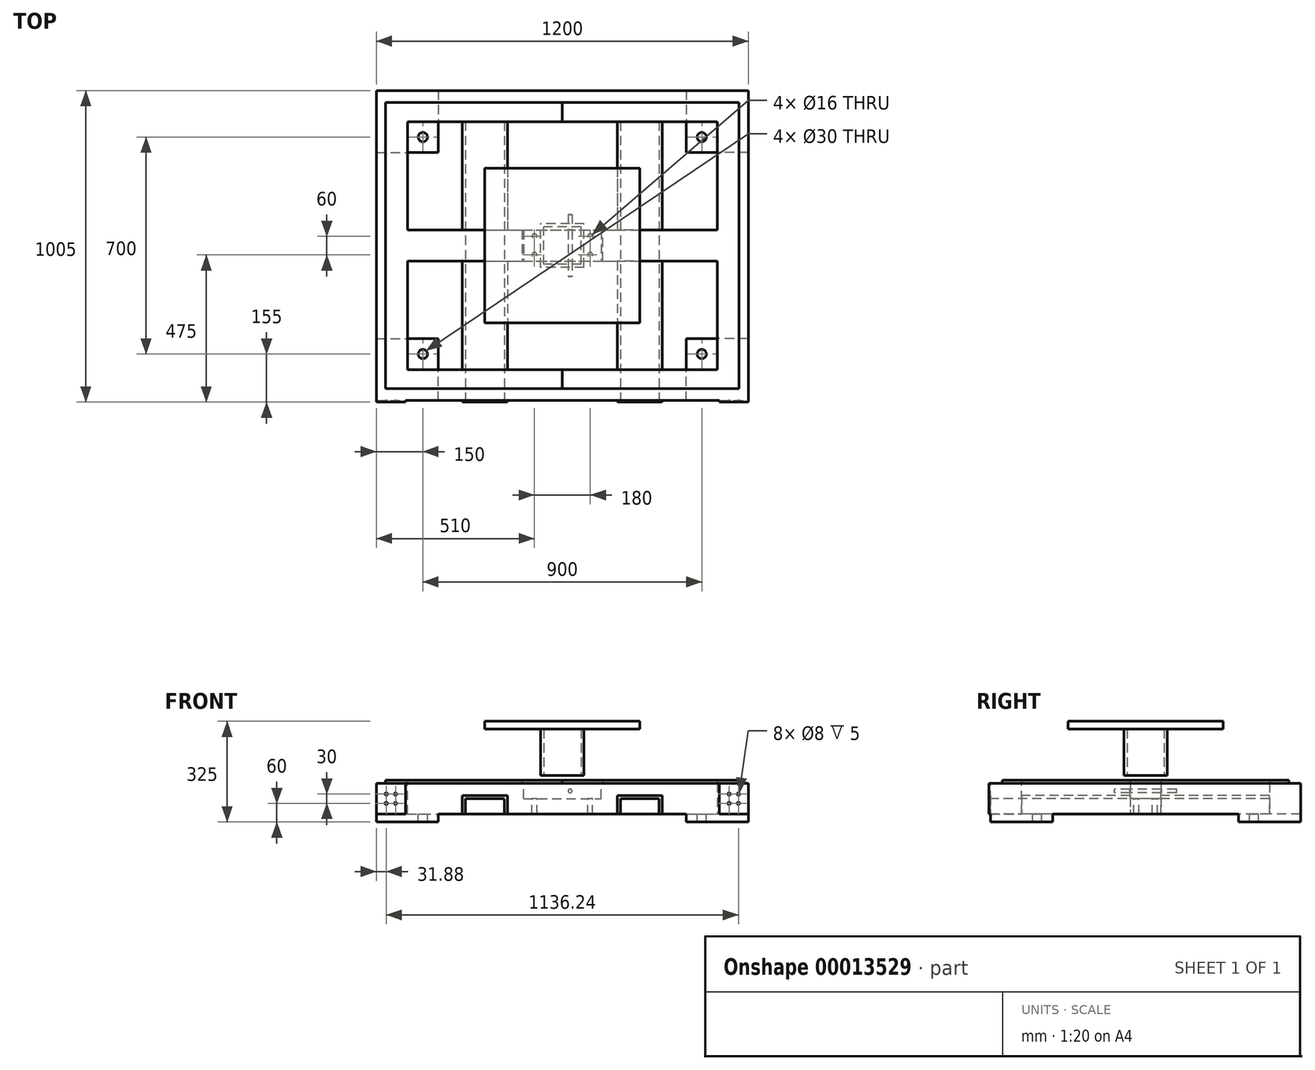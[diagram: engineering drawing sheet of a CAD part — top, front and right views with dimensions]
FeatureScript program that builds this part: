
annotation { "Feature Type Name" : "Feature", "Feature Type Description" : "" }
export const myFeature = defineFeature(function(context is Context, id is Id, definition is map)
    precondition{}
    {
        {
            var Q0;
            Q0=qCreatedBy(makeId("Top.planeOp"),FACE);
            var sketch = newSketch(context, id + "F0", { "sketchPlane" : qUnion([Q0])});
            skLineSegment(sketch, "E0.rect.bottom", {"start": v(-500, 50) * mm, "end": v(500, 50) * mm});
            skLineSegment(sketch, "E0.rect.top", {"start": v(-500, -50) * mm, "end": v(500, -50) * mm});
            skLineSegment(sketch, "E0.rect.left", {"start": v(-500, 50) * mm, "end": v(-500, -50) * mm});
            skLineSegment(sketch, "E0.rect.right", {"start": v(500, 50) * mm, "end": v(500, -50) * mm});
            skPoint(sketch, "E0.rect.middle", {"position": v(0, 0) * mm});
            skLineSegment(sketch, "E1", {"start": v(0, 0) * mm, "end": v(0, 499.4) * mm, "construction": true});
            skLineSegment(sketch, "E2", {"start": v(0, 0) * mm, "end": v(0, -436.12) * mm, "construction": true});
            skLineSegment(sketch, "E3", {"start": v(0, 450) * mm, "end": v(-502.35, 450) * mm, "construction": true});
            skLineSegment(sketch, "E4", {"start": v(0, 0) * mm, "end": v(-500, 0) * mm, "construction": true});
            skLineSegment(sketch, "E5", {"start": v(0, 0) * mm, "end": v(500, 0) * mm, "construction": true});
            skLineSegment(sketch, "E6.0.MirrorCS", {"start": v(0, -450) * mm, "end": v(-502.35, -450) * mm, "construction": true});
            skLineSegment(sketch, "E7.rect.bottom", {"start": v(-500, 400) * mm, "end": v(500, 400) * mm});
            skLineSegment(sketch, "E7.rect.top", {"start": v(-500, 500) * mm, "end": v(500, 500) * mm});
            skLineSegment(sketch, "E7.rect.left", {"start": v(-500, 400) * mm, "end": v(-500, 500) * mm});
            skLineSegment(sketch, "E7.rect.right", {"start": v(500, 400) * mm, "end": v(500, 500) * mm});
            skPoint(sketch, "E7.rect.middle", {"position": v(0, 450) * mm});
            skLineSegment(sketch, "E8.rect.bottom", {"start": v(-500, -400) * mm, "end": v(500, -400) * mm});
            skLineSegment(sketch, "E8.rect.top", {"start": v(-500, -500) * mm, "end": v(500, -500) * mm});
            skLineSegment(sketch, "E8.rect.left", {"start": v(-500, -400) * mm, "end": v(-500, -500) * mm});
            skLineSegment(sketch, "E8.rect.right", {"start": v(500, -400) * mm, "end": v(500, -500) * mm});
            skPoint(sketch, "E8.rect.middle", {"position": v(0, -450) * mm});
            skLineSegment(sketch, "E9", {"start": v(-500, 500) * mm, "end": v(-500, -512.7) * mm, "construction": true});
            skLineSegment(sketch, "E10", {"start": v(500, 500) * mm, "end": v(500, -500) * mm, "construction": true});
            skLineSegment(sketch, "E11", {"start": v(-500, 400) * mm, "end": v(-600, 500) * mm});
            skLineSegment(sketch, "E12", {"start": v(-600, 500) * mm, "end": v(-500, 500) * mm});
            skLineSegment(sketch, "E13.1.MirrorCS", {"start": v(500, 400) * mm, "end": v(600, 500) * mm});
            skLineSegment(sketch, "E13.2.MirrorCS", {"start": v(600, 500) * mm, "end": v(500, 500) * mm});
            skLineSegment(sketch, "E14.1.MirrorCS", {"start": v(-500, -400) * mm, "end": v(-600, -500) * mm});
            skLineSegment(sketch, "E14.2.MirrorCS", {"start": v(-600, -500) * mm, "end": v(-500, -500) * mm});
            skLineSegment(sketch, "E15.1.MirrorCS", {"start": v(500, -400) * mm, "end": v(600, -500) * mm});
            skLineSegment(sketch, "E15.3.MirrorCS", {"start": v(600, -500) * mm, "end": v(500, -500) * mm});
            skLineSegment(sketch, "E16", {"start": v(-600, 500) * mm, "end": v(-600, -500) * mm});
            skLineSegment(sketch, "E17", {"start": v(-500, -400) * mm, "end": v(-500, 400) * mm});
            skLineSegment(sketch, "E18", {"start": v(500, 400) * mm, "end": v(500, -400) * mm});
            skLineSegment(sketch, "E19", {"start": v(600, -500) * mm, "end": v(600, 500) * mm});
            skLineSegment(sketch, "E20", {"start": v(-500, 400) * mm, "end": v(-250, 400) * mm});
            skLineSegment(sketch, "E21", {"start": v(-250, 400) * mm, "end": v(-250, 352.87) * mm});
            skSolve(sketch);
        }
        {
            var Q0;
            {var subQ1=sQuery(id+"F0.wireOp",EDGE,"E11");Q0=makeQuery(id+"F0.imprint","IMPRINT",FACE,{"disambiguationData":[TD([[makeQuery(id+"F0.imprint","IMPRINT",EDGE,{"derivedFrom":subQ1}),1.0]])]});}
            extrude(context, id + "F1", {"entities" : qUnion([Q0]), "endBound" : BoundingType.SYMMETRIC, "oppositeDirection" : true, "depth" : 100 * mm});
        }
        {
            var Q0;
            {var subQ4=sQuery(id+"F0.wireOp",EDGE,"E13.1.MirrorCS");Q0=makeQuery(id+"F0.imprint","IMPRINT",FACE,{"disambiguationData":[TD([[makeQuery(id+"F0.imprint","IMPRINT",EDGE,{"derivedFrom":subQ4}),-1.0]])]});}
            extrude(context, id + "F2", {"entities" : qUnion([Q0]), "endBound" : BoundingType.SYMMETRIC, "depth" : 100 * mm});
        }
        {
            var Q0;
            Q0=makeQuery(id+"F0.imprint","IMPRINT",FACE,{"disambiguationData":[TD([[makeQuery(id+"F0.imprint","IMPRINT",EDGE,{"derivedFrom":sQuery(id+"F0.wireOp",EDGE,"E8.rect.bottom")}),-1.0]])]});
            var Q1;
            Q1=makeQuery(id+"F0.imprint","IMPRINT",FACE,{"disambiguationData":[TD([[makeQuery(id+"F0.imprint","IMPRINT",EDGE,{"derivedFrom":sQuery(id+"F0.wireOp",EDGE,"E8.rect.left")}),-1.0]])]});
            var Q2;
            Q2=makeQuery(id+"F0.imprint","IMPRINT",FACE,{"disambiguationData":[TD([[makeQuery(id+"F0.imprint","IMPRINT",EDGE,{"derivedFrom":sQuery(id+"F0.wireOp",EDGE,"E15.1.MirrorCS")}),-1.0]])]});
            extrude(context, id + "F3", {"entities" : qUnion([Q0, Q1, Q2]), "endBound" : BoundingType.SYMMETRIC, "depth" : 100 * mm});
        }
        {
            var Q0;
            Q0=makeQuery(id+"F0.imprint","IMPRINT",FACE,{"disambiguationData":[TD([[makeQuery(id+"F0.imprint","IMPRINT",EDGE,{"derivedFrom":sQuery(id+"F0.wireOp",EDGE,"E7.rect.bottom")}),1.0]])]});
            var Q1;
            Q1=makeQuery(id+"F0.imprint","IMPRINT",FACE,{"disambiguationData":[TD([[makeQuery(id+"F0.imprint","IMPRINT",EDGE,{"derivedFrom":sQuery(id+"F0.wireOp",EDGE,"E7.rect.left")}),1.0]])]});
            var Q2;
            Q2=makeQuery(id+"F0.imprint","IMPRINT",FACE,{"disambiguationData":[TD([[makeQuery(id+"F0.imprint","IMPRINT",EDGE,{"derivedFrom":sQuery(id+"F0.wireOp",EDGE,"E7.rect.right")}),-1.0]])]});
            extrude(context, id + "F4", {"entities" : qUnion([Q0, Q1, Q2]), "endBound" : BoundingType.SYMMETRIC, "depth" : 100 * mm});
        }
        {
            var Q0;
            {var subQ2=sQuery(id+"F0.wireOp",EDGE,"E0.rect.bottom");Q0=makeQuery(id+"F0.imprint","IMPRINT",FACE,{"disambiguationData":[TD([[makeQuery(id+"F0.imprint","IMPRINT",EDGE,{"derivedFrom":subQ2}),-1.0]])]});}
            extrude(context, id + "F5", {"entities" : qUnion([Q0]), "endBound" : BoundingType.SYMMETRIC, "depth" : 100 * mm});
        }
        {
            var Q0;
            Q0=makeQuery(id+"F3.opExtrude","SWEPT_FACE",FACE,{"disambiguationData":[OSD([sQuery(id+"F0.wireOp",EDGE,"E8.rect.top"),sQuery(id+"F0.wireOp",EDGE,"E14.2.MirrorCS"),sQuery(id+"F0.wireOp",EDGE,"E15.3.MirrorCS")])]});
            var sketch = newSketch(context, id + "F6", { "sketchPlane" : qUnion([Q0])});
            skLineSegment(sketch, "E22", {"start": v(-187.5, -50) * mm, "end": v(-187.5, 0) * mm});
            skLineSegment(sketch, "E23", {"start": v(-187.5, 0) * mm, "end": v(-312.5, 0) * mm});
            skLineSegment(sketch, "E24", {"start": v(-312.5, 0) * mm, "end": v(-312.5, -50) * mm});
            skLineSegment(sketch, "E25.0", {"start": v(-322.5, 0) * mm, "end": v(-322.5, -50) * mm});
            skLineSegment(sketch, "E26.0", {"start": v(-177.5, -50) * mm, "end": v(-177.5, 0) * mm});
            skLineSegment(sketch, "E27", {"start": v(-322.5, 0) * mm, "end": v(-322.5, 10) * mm});
            skLineSegment(sketch, "E28", {"start": v(-177.5, 0) * mm, "end": v(-177.5, 10) * mm});
            skLineSegment(sketch, "E29", {"start": v(-322.5, -50) * mm, "end": v(-312.5, -50) * mm});
            skLineSegment(sketch, "E30", {"start": v(-187.5, -50) * mm, "end": v(-177.5, -50) * mm});
            skLineSegment(sketch, "E31", {"start": v(-177.5, 10) * mm, "end": v(-322.5, 10) * mm});
            skLineSegment(sketch, "E32", {"start": v(0, -50) * mm, "end": v(0, 50) * mm, "construction": true});
            skLineSegment(sketch, "E33.0.MirrorCS", {"start": v(177.5, 0) * mm, "end": v(177.5, 10) * mm});
            skLineSegment(sketch, "E33.1.MirrorCS", {"start": v(322.5, 0) * mm, "end": v(322.5, 10) * mm});
            skLineSegment(sketch, "E33.2.MirrorCS", {"start": v(322.5, -50) * mm, "end": v(312.5, -50) * mm});
            skLineSegment(sketch, "E33.3.MirrorCS", {"start": v(187.5, -50) * mm, "end": v(177.5, -50) * mm});
            skLineSegment(sketch, "E33.4.MirrorCS", {"start": v(322.5, 0) * mm, "end": v(322.5, -50) * mm});
            skLineSegment(sketch, "E33.5.MirrorCS", {"start": v(312.5, 0) * mm, "end": v(312.5, -50) * mm});
            skLineSegment(sketch, "E33.6.MirrorCS", {"start": v(177.5, 10) * mm, "end": v(322.5, 10) * mm});
            skLineSegment(sketch, "E33.7.MirrorCS", {"start": v(187.5, 0) * mm, "end": v(312.5, 0) * mm});
            skLineSegment(sketch, "E33.8.MirrorCS", {"start": v(187.5, -50) * mm, "end": v(187.5, 0) * mm});
            skLineSegment(sketch, "E33.9.MirrorCS", {"start": v(177.5, -50) * mm, "end": v(177.5, 0) * mm});
            skSolve(sketch);
        }
        {
            var Q0;
            {var subQ2=sQuery(id+"F6.wireOp",EDGE,"E22");Q0=makeQuery(id+"F6.imprint","IMPRINT",FACE,{"disambiguationData":[TD([[makeQuery(id+"F6.imprint","IMPRINT",EDGE,{"derivedFrom":subQ2}),1.0]])]});}
            var Q1;
            {var subQ2=sQuery(id+"F6.wireOp",EDGE,"E33.5.MirrorCS");Q1=makeQuery(id+"F6.imprint","IMPRINT",FACE,{"disambiguationData":[TD([[makeQuery(id+"F6.imprint","IMPRINT",EDGE,{"derivedFrom":subQ2}),-1.0]])]});}
            var Q2;
            Q2=makeQuery(id+"F4.opExtrude","SWEPT_FACE",FACE,{"disambiguationData":[OSD([sQuery(id+"F0.wireOp",EDGE,"E7.rect.bottom"),sQuery(id+"F0.wireOp",EDGE,"E20")])]});
            extrude(context, id + "F7", {"entities" : qUnion([Q0, Q1]), "operationType" : NewBodyOperationType.REMOVE, "endBound" : BoundingType.UP_TO_SURFACE, "oppositeDirection" : true, "endBoundEntityFace" : qUnion([Q2]), "depth" : mm});
        }
        {
            var Q0;
            Q0=makeQuery(id+"F6.imprint","IMPRINT",FACE,{"disambiguationData":[TD([[makeQuery(id+"F6.imprint","IMPRINT",EDGE,{"derivedFrom":sQuery(id+"F6.wireOp",EDGE,"E33.0.MirrorCS")}),-1.0]])]});
            var Q1;
            Q1=makeQuery(id+"F6.imprint","IMPRINT",FACE,{"disambiguationData":[TD([[makeQuery(id+"F6.imprint","IMPRINT",EDGE,{"derivedFrom":sQuery(id+"F6.wireOp",EDGE,"E22")}),-1.0]])]});
            var Q2;
            Q2=makeQuery(id+"F4.opExtrude","SWEPT_FACE",FACE,{"disambiguationData":[OSD([sQuery(id+"F0.wireOp",EDGE,"E7.rect.bottom"),sQuery(id+"F0.wireOp",EDGE,"E20")])]});
            extrude(context, id + "F8", {"entities" : qUnion([Q0, Q1]), "endBound" : BoundingType.UP_TO_SURFACE, "oppositeDirection" : true, "endBoundEntityFace" : qUnion([Q2]), "depth" : 25 * mm, "hasSecondDirection" : true, "secondDirectionOppositeDirection" : false, "secondDirectionDepth" : 5 * mm});
        }
        {
            var Q0;
            Q0=makeQuery(id+"F8.opExtrude","SWEPT_BODY",BODY,{"disambiguationData":[OSD([sQuery(id+"F6.wireOp",EDGE,"E22"),sQuery(id+"F6.wireOp",EDGE,"E23"),sQuery(id+"F6.wireOp",EDGE,"E24"),sQuery(id+"F6.wireOp",EDGE,"E25.0"),sQuery(id+"F6.wireOp",EDGE,"E26.0"),sQuery(id+"F6.wireOp",EDGE,"E27"),sQuery(id+"F6.wireOp",EDGE,"E28"),sQuery(id+"F6.wireOp",EDGE,"E29"),sQuery(id+"F6.wireOp",EDGE,"E30"),sQuery(id+"F6.wireOp",EDGE,"E31")])]});
            var Q1;
            Q1=qCreatedBy(makeId("Right.planeOp"),FACE);
            mirror(context, id + "F9", {"operationType" : NewBodyOperationType.ADD, "entities" : qUnion([Q0]), "mirrorPlane" : qUnion([Q1])});
        }
        {
            var Q0;
            {var subQ0=sQuery(id+"F6.wireOp",EDGE,"E23");var subQ1=sQuery(id+"F6.wireOp",EDGE,"E24");var subQ2=makeQuery(id+"F7.opExtrude","SWEPT_EDGE",EDGE,{"disambiguationData":[OSD([subQ0,subQ1])]});Q0=makeQuery(id+"F9.boolean.opBoolean","MERGE",EDGE,{"derivedFrom":[makeQuery(id+"F7.boolean.opBoolean","COPY",EDGE,{"disambiguationData":[OD(0.0)],"derivedFrom":subQ2}),makeQuery(id+"F7.boolean.opBoolean","COPY",EDGE,{"disambiguationData":[OD(1.0)],"derivedFrom":subQ2}),makeQuery(id+"F8.opExtrude","SWEPT_EDGE",EDGE,{"disambiguationData":[OSD([subQ0,subQ1])]})]});}
            var Q1;
            {var subQ0=sQuery(id+"F6.wireOp",EDGE,"E22");var subQ1=sQuery(id+"F6.wireOp",EDGE,"E23");var subQ2=makeQuery(id+"F7.opExtrude","SWEPT_EDGE",EDGE,{"disambiguationData":[OSD([subQ0,subQ1])]});Q1=makeQuery(id+"F9.boolean.opBoolean","MERGE",EDGE,{"derivedFrom":[makeQuery(id+"F7.boolean.opBoolean","COPY",EDGE,{"disambiguationData":[OD(0.0)],"derivedFrom":subQ2}),makeQuery(id+"F7.boolean.opBoolean","COPY",EDGE,{"disambiguationData":[OD(1.0)],"derivedFrom":subQ2}),makeQuery(id+"F8.opExtrude","SWEPT_EDGE",EDGE,{"disambiguationData":[OSD([subQ0,subQ1])]})]});}
            var Q2;
            {var subQ0=makeQuery(id+"F7.opExtrude","SWEPT_EDGE",EDGE,{"disambiguationData":[OSD([sQuery(id+"F6.wireOp",EDGE,"E33.7.MirrorCS"),sQuery(id+"F6.wireOp",EDGE,"E33.8.MirrorCS")])]});Q2=makeQuery(id+"F9.boolean.opBoolean","MERGE",EDGE,{"derivedFrom":[makeQuery(id+"F7.boolean.opBoolean","COPY",EDGE,{"disambiguationData":[OD(0.0)],"derivedFrom":subQ0}),makeQuery(id+"F7.boolean.opBoolean","COPY",EDGE,{"disambiguationData":[OD(1.0)],"derivedFrom":subQ0}),makeQuery(id+"F9.opPattern","COPY",EDGE,{"derivedFrom":makeQuery(id+"F8.opExtrude","SWEPT_EDGE",EDGE,{"disambiguationData":[OSD([sQuery(id+"F6.wireOp",EDGE,"E22"),sQuery(id+"F6.wireOp",EDGE,"E23")])]}),"instanceName":"1"})]});}
            var Q3;
            {var subQ0=makeQuery(id+"F7.opExtrude","SWEPT_EDGE",EDGE,{"disambiguationData":[OSD([sQuery(id+"F6.wireOp",EDGE,"E33.5.MirrorCS"),sQuery(id+"F6.wireOp",EDGE,"E33.7.MirrorCS")])]});Q3=makeQuery(id+"F9.boolean.opBoolean","MERGE",EDGE,{"derivedFrom":[makeQuery(id+"F7.boolean.opBoolean","COPY",EDGE,{"disambiguationData":[OD(0.0)],"derivedFrom":subQ0}),makeQuery(id+"F7.boolean.opBoolean","COPY",EDGE,{"disambiguationData":[OD(1.0)],"derivedFrom":subQ0}),makeQuery(id+"F9.opPattern","COPY",EDGE,{"derivedFrom":makeQuery(id+"F8.opExtrude","SWEPT_EDGE",EDGE,{"disambiguationData":[OSD([sQuery(id+"F6.wireOp",EDGE,"E23"),sQuery(id+"F6.wireOp",EDGE,"E24")])]}),"instanceName":"1"})]});}
            fillet(context, id + "F10", {"entities" : qUnion([Q0, Q1, Q2, Q3]), "radius" : 3 * mm, "allowEdgeOverflow" : false});
        }
        {
            var Q0;
            {var subQ0=sQuery(id+"F0.wireOp",EDGE,"E8.rect.bottom");var subQ1=sQuery(id+"F0.wireOp",EDGE,"E8.rect.top");var subQ2=sQuery(id+"F0.wireOp",EDGE,"E14.1.MirrorCS");var subQ3=sQuery(id+"F0.wireOp",EDGE,"E14.2.MirrorCS");var subQ4=sQuery(id+"F0.wireOp",EDGE,"E15.3.MirrorCS");Q0=makeQuery(id+"F7.boolean.opBoolean","SPLIT",FACE,{"disambiguationData":[TD([makeQuery(id+"F3.opExtrude","SWEPT_FACE",FACE,{"disambiguationData":[OSD([subQ2])]})])],"derivedFrom":makeQuery(id+"F3.opExtrude","CAP_FACE",FACE,{"disambiguationData":[OSD([subQ0,subQ1,subQ2,subQ3,sQuery(id+"F0.wireOp",EDGE,"E15.1.MirrorCS"),subQ4])],"isStart":true})});}
            var sketch = newSketch(context, id + "F11", { "sketchPlane" : qUnion([Q0])});
            skLineSegment(sketch, "E34", {"start": v(0, 0) * mm, "end": v(0, 500) * mm, "construction": true});
            skLineSegment(sketch, "E35", {"start": v(0, 0) * mm, "end": v(-600, 0) * mm, "construction": true});
            skLineSegment(sketch, "E36.bottom", {"start": v(-600, 500) * mm, "end": v(-400, 500) * mm});
            skLineSegment(sketch, "E36.top", {"start": v(-600, 300) * mm, "end": v(-400, 300) * mm});
            skLineSegment(sketch, "E36.left", {"start": v(-600, 500) * mm, "end": v(-600, 300) * mm});
            skLineSegment(sketch, "E36.right", {"start": v(-400, 500) * mm, "end": v(-400, 300) * mm});
            skLineSegment(sketch, "E37.0.MirrorCS", {"start": v(400, 500) * mm, "end": v(400, 300) * mm});
            skLineSegment(sketch, "E37.1.MirrorCS", {"start": v(600, 500) * mm, "end": v(400, 500) * mm});
            skLineSegment(sketch, "E37.2.MirrorCS", {"start": v(600, 500) * mm, "end": v(600, 300) * mm});
            skLineSegment(sketch, "E37.3.MirrorCS", {"start": v(600, 300) * mm, "end": v(400, 300) * mm});
            skLineSegment(sketch, "E38.0.MirrorCS", {"start": v(0, 0) * mm, "end": v(600, 0) * mm, "construction": true});
            skLineSegment(sketch, "E39.0.MirrorCS", {"start": v(-600, -500) * mm, "end": v(-600, -300) * mm});
            skLineSegment(sketch, "E39.1.MirrorCS", {"start": v(600, -500) * mm, "end": v(600, -300) * mm});
            skLineSegment(sketch, "E39.2.MirrorCS", {"start": v(-600, -500) * mm, "end": v(-400, -500) * mm});
            skLineSegment(sketch, "E39.3.MirrorCS", {"start": v(400, -500) * mm, "end": v(400, -300) * mm});
            skLineSegment(sketch, "E39.4.MirrorCS", {"start": v(600, -300) * mm, "end": v(400, -300) * mm});
            skLineSegment(sketch, "E39.5.MirrorCS", {"start": v(600, -500) * mm, "end": v(400, -500) * mm});
            skLineSegment(sketch, "E39.6.MirrorCS", {"start": v(-400, -500) * mm, "end": v(-400, -300) * mm});
            skLineSegment(sketch, "E39.7.MirrorCS", {"start": v(600, -300) * mm, "end": v(400, -300) * mm});
            skLineSegment(sketch, "E39.8.MirrorCS", {"start": v(-600, -300) * mm, "end": v(-400, -300) * mm});
            skLineSegment(sketch, "E39.9.MirrorCS", {"start": v(400, -500) * mm, "end": v(400, -300) * mm});
            skLineSegment(sketch, "E39.10.MirrorCS", {"start": v(600, -500) * mm, "end": v(400, -500) * mm});
            skLineSegment(sketch, "E39.11.MirrorCS", {"start": v(-600, -500) * mm, "end": v(-400, -500) * mm});
            skLineSegment(sketch, "E39.12.MirrorCS", {"start": v(-600, -300) * mm, "end": v(-400, -300) * mm});
            skLineSegment(sketch, "E39.13.MirrorCS", {"start": v(600, -500) * mm, "end": v(600, -300) * mm});
            skLineSegment(sketch, "E39.14.MirrorCS", {"start": v(-600, -500) * mm, "end": v(-600, -300) * mm});
            skLineSegment(sketch, "E39.15.MirrorCS", {"start": v(-400, -500) * mm, "end": v(-400, -300) * mm});
            skLineSegment(sketch, "E40", {"start": v(-500, 400) * mm, "end": v(-400, 300) * mm, "construction": true});
            skLineSegment(sketch, "E41", {"start": v(-400, 400) * mm, "end": v(-500, 300) * mm, "construction": true});
            skCircle(sketch, "E42", {"center": v(-450, 350) * mm, "radius": 15 * mm});
            skLineSegment(sketch, "E43.0.MirrorCS", {"start": v(400, 400) * mm, "end": v(500, 300) * mm, "construction": true});
            skCircle(sketch, "E43.1.MirrorC", {"center": v(450, 350) * mm, "radius": 15 * mm});
            skCircle(sketch, "E44.1.MirrorC", {"center": v(450, -350) * mm, "radius": 15 * mm});
            skLineSegment(sketch, "E44.3.MirrorCS", {"start": v(-400, -400) * mm, "end": v(-500, -300) * mm, "construction": true});
            skCircle(sketch, "E44.4.MirrorC", {"center": v(-450, -350) * mm, "radius": 15 * mm});
            skLineSegment(sketch, "E44.6.MirrorCS", {"start": v(-500, -400) * mm, "end": v(-400, -300) * mm, "construction": true});
            skLineSegment(sketch, "E44.8.MirrorCS", {"start": v(400, -400) * mm, "end": v(500, -300) * mm, "construction": true});
            skSolve(sketch);
        }
        {
            var Q0;
            Q0=qSketchRegion(id+"F11",true);
            extrude(context, id + "F12", {"entities" : qUnion([Q0]), "operationType" : NewBodyOperationType.ADD, "depth" : 25 * mm});
        }
        {
            var Q0;
            {var subQ9=sQuery(id+"F6.wireOp",EDGE,"E25.0");Q0=makeQuery(id+"F6.imprint","IMPRINT",FACE,{"disambiguationData":[TD([[makeQuery(id+"F6.imprint","IMPRINT",EDGE,{"derivedFrom":subQ9}),-1.0]])]});}
            var sketch = newSketch(context, id + "F13", { "sketchPlane" : qUnion([Q0])});
            skLineSegment(sketch, "E45.right", {"start": v(-600, -50) * mm, "end": v(-600, 0) * mm});
            skPoint(sketch, "E46.rect.middle", {"position": v(-553.12, 0) * mm});
            skCircle(sketch, "E47", {"center": v(-568.12, 15) * mm, "radius": 4 * mm});
            skCircle(sketch, "E48", {"center": v(-538.12, 15) * mm, "radius": 4 * mm});
            skCircle(sketch, "E49", {"center": v(-568.12, -15) * mm, "radius": 4 * mm});
            skCircle(sketch, "E50", {"center": v(-538.12, -15) * mm, "radius": 4 * mm});
            skCircle(sketch, "E51.0.MirrorC", {"center": v(568.12, -15) * mm, "radius": 4 * mm});
            skCircle(sketch, "E51.1.MirrorC", {"center": v(538.12, 15) * mm, "radius": 4 * mm});
            skCircle(sketch, "E51.3.MirrorC", {"center": v(568.12, 15) * mm, "radius": 4 * mm});
            skCircle(sketch, "E51.4.MirrorC", {"center": v(538.12, -15) * mm, "radius": 4 * mm});
            skPoint(sketch, "E51.6.MirrorP", {"position": v(553.12, 0) * mm});
            skLineSegment(sketch, "E52.rect.bottom", {"start": v(-600, -50) * mm, "end": v(-506.24, -50) * mm});
            skLineSegment(sketch, "E52.rect.top", {"start": v(-600, 50) * mm, "end": v(-506.24, 50) * mm});
            skLineSegment(sketch, "E52.rect.left", {"start": v(-600, -50) * mm, "end": v(-600, 50) * mm});
            skLineSegment(sketch, "E52.rect.right", {"start": v(-506.24, -50) * mm, "end": v(-506.24, 50) * mm});
            skLineSegment(sketch, "E53.2.MirrorCS", {"start": v(600, -50) * mm, "end": v(600, 0) * mm});
            skLineSegment(sketch, "E53.3.MirrorCS", {"start": v(600, 50) * mm, "end": v(506.24, 50) * mm});
            skLineSegment(sketch, "E53.4.MirrorCS", {"start": v(600, -50) * mm, "end": v(506.24, -50) * mm});
            skLineSegment(sketch, "E53.6.MirrorCS", {"start": v(506.24, -50) * mm, "end": v(506.24, 50) * mm});
            skLineSegment(sketch, "E53.10.MirrorCS", {"start": v(600, -50) * mm, "end": v(600, 50) * mm});
            skSolve(sketch);
        }
        {
            var Q0;
            Q0=qSketchRegion(id+"F13",true);
            extrude(context, id + "F14", {"entities" : qUnion([Q0]), "operationType" : NewBodyOperationType.ADD, "depth" : 5 * mm});
        }
        {
            var Q0;
            Q0=makeQuery(id+"F5.opExtrude","CAP_FACE",FACE,{"disambiguationData":[OSD([sQuery(id+"F0.wireOp",EDGE,"E0.rect.bottom"),sQuery(id+"F0.wireOp",EDGE,"E0.rect.top"),sQuery(id+"F0.wireOp",EDGE,"E17"),sQuery(id+"F0.wireOp",EDGE,"E18")])],"isStart":false});
            var sketch = newSketch(context, id + "F15", { "sketchPlane" : qUnion([Q0])});
            skLineSegment(sketch, "E54.rect.bottom", {"start": v(125, 100) * mm, "end": v(-125, 100) * mm});
            skLineSegment(sketch, "E54.rect.top", {"start": v(125, -100) * mm, "end": v(-125, -100) * mm});
            skLineSegment(sketch, "E54.rect.left", {"start": v(125, 100) * mm, "end": v(125, -100) * mm});
            skLineSegment(sketch, "E54.rect.right", {"start": v(-125, 100) * mm, "end": v(-125, -100) * mm});
            skPoint(sketch, "E54.rect.middle", {"position": v(0, 0) * mm});
            skCircle(sketch, "E55", {"center": v(-59.74, 25) * mm, "radius": 7.5 * mm});
            skCircle(sketch, "E56.0.MirrorC", {"center": v(-59.74, -25) * mm, "radius": 7.5 * mm});
            skCircle(sketch, "E57.1.MirrorC", {"center": v(59.74, 25) * mm, "radius": 7.5 * mm});
            skCircle(sketch, "E57.4.MirrorC", {"center": v(59.74, -25) * mm, "radius": 7.5 * mm});
            skSolve(sketch);
        }
        {
            var Q0;
            Q0=qSketchRegion(id+"F15",true);
            var Q1;
            Q1=makeQuery(id+"F15.imprint","IMPRINT",FACE,{"disambiguationData":[TD([[makeQuery(id+"F15.imprint","IMPRINT",EDGE,{"derivedFrom":sQuery(id+"F15.wireOp",EDGE,"E55")}),1.0]])]});
            var Q2;
            Q2=makeQuery(id+"F15.imprint","IMPRINT",FACE,{"disambiguationData":[TD([[makeQuery(id+"F15.imprint","IMPRINT",EDGE,{"derivedFrom":sQuery(id+"F15.wireOp",EDGE,"E57.1.MirrorC")}),-1.0]])]});
            var Q3;
            Q3=makeQuery(id+"F15.imprint","IMPRINT",FACE,{"disambiguationData":[TD([[makeQuery(id+"F15.imprint","IMPRINT",EDGE,{"derivedFrom":sQuery(id+"F15.wireOp",EDGE,"E57.4.MirrorC")}),1.0]])]});
            var Q4;
            Q4=makeQuery(id+"F15.imprint","IMPRINT",FACE,{"disambiguationData":[TD([[makeQuery(id+"F15.imprint","IMPRINT",EDGE,{"derivedFrom":sQuery(id+"F15.wireOp",EDGE,"E56.0.MirrorC")}),-1.0]])]});
            extrude(context, id + "F16", {"entities" : qUnion([Q0, Q1, Q2, Q3, Q4]), "depth" : 25 * mm});
        }
        {
            var Q0;
            Q0=makeQuery(id+"F16.opExtrude","CAP_FACE",FACE,{"disambiguationData":[OSD([sQuery(id+"F15.wireOp",EDGE,"E54.rect.bottom"),sQuery(id+"F15.wireOp",EDGE,"E54.rect.top"),sQuery(id+"F15.wireOp",EDGE,"E54.rect.left"),sQuery(id+"F15.wireOp",EDGE,"E54.rect.right")])],"isStart":false});
            var sketch = newSketch(context, id + "F17", { "sketchPlane" : qUnion([Q0])});
            skLineSegment(sketch, "E58.rect.bottom", {"start": v(-125, -100) * mm, "end": v(125, -100) * mm});
            skLineSegment(sketch, "E58.rect.top", {"start": v(-125, 100) * mm, "end": v(125, 100) * mm});
            skLineSegment(sketch, "E58.rect.left", {"start": v(-125, -100) * mm, "end": v(-125, 100) * mm});
            skLineSegment(sketch, "E58.rect.right", {"start": v(125, -100) * mm, "end": v(125, 100) * mm});
            skPoint(sketch, "E58.rect.middle", {"position": v(0, 0) * mm});
            skLineSegment(sketch, "E59.rect.bottom", {"start": v(-90, 30) * mm, "end": v(90, 30) * mm, "construction": true});
            skLineSegment(sketch, "E59.rect.top", {"start": v(-90, -30) * mm, "end": v(90, -30) * mm, "construction": true});
            skLineSegment(sketch, "E59.rect.left", {"start": v(-90, 30) * mm, "end": v(-90, -30) * mm, "construction": true});
            skLineSegment(sketch, "E59.rect.right", {"start": v(90, 30) * mm, "end": v(90, -30) * mm, "construction": true});
            skCircle(sketch, "E60", {"center": v(-90, 30) * mm, "radius": 8 * mm});
            skCircle(sketch, "E61", {"center": v(-90, -30) * mm, "radius": 8 * mm});
            skCircle(sketch, "E62", {"center": v(90, 30) * mm, "radius": 8 * mm});
            skCircle(sketch, "E63", {"center": v(90, -30) * mm, "radius": 8 * mm});
            skSolve(sketch);
        }
        {
            var Q0;
            Q0=makeQuery(id+"F17.imprint","IMPRINT",FACE,{"disambiguationData":[TD([[makeQuery(id+"F17.imprint","IMPRINT",EDGE,{"derivedFrom":sQuery(id+"F17.wireOp",EDGE,"E60")}),1.0]])]});
            var Q1;
            Q1=makeQuery(id+"F17.imprint","IMPRINT",FACE,{"disambiguationData":[TD([[makeQuery(id+"F17.imprint","IMPRINT",EDGE,{"derivedFrom":sQuery(id+"F17.wireOp",EDGE,"E61")}),1.0]])]});
            var Q2;
            Q2=makeQuery(id+"F17.imprint","IMPRINT",FACE,{"disambiguationData":[TD([[makeQuery(id+"F17.imprint","IMPRINT",EDGE,{"derivedFrom":sQuery(id+"F17.wireOp",EDGE,"E62")}),1.0]])]});
            var Q3;
            Q3=makeQuery(id+"F17.imprint","IMPRINT",FACE,{"disambiguationData":[TD([[makeQuery(id+"F17.imprint","IMPRINT",EDGE,{"derivedFrom":sQuery(id+"F17.wireOp",EDGE,"E63")}),1.0]])]});
            extrude(context, id + "F18", {"entities" : qUnion([Q0, Q1, Q2, Q3]), "operationType" : NewBodyOperationType.REMOVE, "endBound" : BoundingType.THROUGH_ALL, "oppositeDirection" : true, "depth" : 25 * mm});
        }
        {
            var Q0;
            Q0=makeQuery(id+"F16.opExtrude","CAP_FACE",FACE,{"disambiguationData":[OSD([sQuery(id+"F15.wireOp",EDGE,"E54.rect.bottom"),sQuery(id+"F15.wireOp",EDGE,"E54.rect.top"),sQuery(id+"F15.wireOp",EDGE,"E54.rect.left"),sQuery(id+"F15.wireOp",EDGE,"E54.rect.right")])],"isStart":false});
            var sketch = newSketch(context, id + "F19", { "sketchPlane" : qUnion([Q0])});
            skLineSegment(sketch, "E64.rect.bottom", {"start": v(60, -60) * mm, "end": v(-60, -60) * mm});
            skLineSegment(sketch, "E64.rect.top", {"start": v(60, 60) * mm, "end": v(-60, 60) * mm});
            skLineSegment(sketch, "E64.rect.left", {"start": v(60, -60) * mm, "end": v(60, 60) * mm});
            skLineSegment(sketch, "E64.rect.right", {"start": v(-60, -60) * mm, "end": v(-60, 60) * mm});
            skPoint(sketch, "E64.rect.middle", {"position": v(0, 0) * mm});
            skLineSegment(sketch, "E65.rect.bottom", {"start": v(70, -70) * mm, "end": v(-70, -70) * mm});
            skLineSegment(sketch, "E65.rect.top", {"start": v(70, 70) * mm, "end": v(-70, 70) * mm});
            skLineSegment(sketch, "E65.rect.left", {"start": v(70, -70) * mm, "end": v(70, 70) * mm});
            skLineSegment(sketch, "E65.rect.right", {"start": v(-70, -70) * mm, "end": v(-70, 70) * mm});
            skSolve(sketch);
        }
        {
            var Q0;
            Q0=qSketchRegion(id+"F19",true);
            extrude(context, id + "F20", {"entities" : qUnion([Q0]), "operationType" : NewBodyOperationType.ADD, "depth" : 150 * mm});
        }
        {
            var Q0;
            Q0=makeQuery(id+"F20.opExtrude","CAP_FACE",FACE,{"disambiguationData":[OSD([sQuery(id+"F19.wireOp",EDGE,"E64.rect.bottom"),sQuery(id+"F19.wireOp",EDGE,"E64.rect.top"),sQuery(id+"F19.wireOp",EDGE,"E64.rect.left"),sQuery(id+"F19.wireOp",EDGE,"E64.rect.right"),sQuery(id+"F19.wireOp",EDGE,"E65.rect.bottom"),sQuery(id+"F19.wireOp",EDGE,"E65.rect.top"),sQuery(id+"F19.wireOp",EDGE,"E65.rect.left"),sQuery(id+"F19.wireOp",EDGE,"E65.rect.right")])],"isStart":false});
            var sketch = newSketch(context, id + "F21", { "sketchPlane" : qUnion([Q0])});
            skLineSegment(sketch, "E66.rect.bottom", {"start": v(250, -250) * mm, "end": v(-250, -250) * mm});
            skLineSegment(sketch, "E66.rect.top", {"start": v(250, 250) * mm, "end": v(-250, 250) * mm});
            skLineSegment(sketch, "E66.rect.left", {"start": v(250, -250) * mm, "end": v(250, 250) * mm});
            skLineSegment(sketch, "E66.rect.right", {"start": v(-250, -250) * mm, "end": v(-250, 250) * mm});
            skPoint(sketch, "E66.rect.middle", {"position": v(0, 0) * mm});
            skSolve(sketch);
        }
        {
            var Q0;
            Q0=qSketchRegion(id+"F21",true);
            extrude(context, id + "F22", {"entities" : qUnion([Q0]), "operationType" : NewBodyOperationType.ADD, "depth" : 25 * mm});
        }
        {
            var Q0;
            Q0=makeQuery(id+"F16.opExtrude","CAP_FACE",FACE,{"disambiguationData":[OSD([sQuery(id+"F15.wireOp",EDGE,"E54.rect.bottom"),sQuery(id+"F15.wireOp",EDGE,"E54.rect.top"),sQuery(id+"F15.wireOp",EDGE,"E54.rect.left"),sQuery(id+"F15.wireOp",EDGE,"E54.rect.right")])],"isStart":true});
            var sketch = newSketch(context, id + "F23", { "sketchPlane" : qUnion([Q0])});
            skLineSegment(sketch, "E67.bottom", {"start": v(-125, 100) * mm, "end": v(125, 100) * mm});
            skLineSegment(sketch, "E67.top", {"start": v(-125, 50.58) * mm, "end": v(125, 50.58) * mm});
            skLineSegment(sketch, "E67.left", {"start": v(-125, 100) * mm, "end": v(-125, 50.58) * mm});
            skLineSegment(sketch, "E67.right", {"start": v(125, 100) * mm, "end": v(125, 50.58) * mm});
            skLineSegment(sketch, "E68.0.MirrorCS", {"start": v(125, -100) * mm, "end": v(125, -50.58) * mm});
            skLineSegment(sketch, "E68.1.MirrorCS", {"start": v(-125, -100) * mm, "end": v(125, -100) * mm});
            skLineSegment(sketch, "E68.2.MirrorCS", {"start": v(-125, -50.58) * mm, "end": v(125, -50.58) * mm});
            skLineSegment(sketch, "E68.3.MirrorCS", {"start": v(-125, -100) * mm, "end": v(-125, -50.58) * mm});
            skSolve(sketch);
        }
        {
            var Q0;
            Q0=makeQuery(id+"F23.imprint","IMPRINT",FACE,{"disambiguationData":[TD([[makeQuery(id+"F23.imprint","IMPRINT",EDGE,{"derivedFrom":sQuery(id+"F23.wireOp",EDGE,"E67.bottom")}),1.0]])]});
            var Q1;
            Q1=makeQuery(id+"F23.imprint","IMPRINT",FACE,{"disambiguationData":[TD([[makeQuery(id+"F23.imprint","IMPRINT",EDGE,{"derivedFrom":sQuery(id+"F23.wireOp",EDGE,"E68.0.MirrorCS")}),1.0]])]});
            extrude(context, id + "F24", {"entities" : qUnion([Q0, Q1]), "operationType" : NewBodyOperationType.ADD, "depth" : 50 * mm});
        }
        {
            var Q0;
            Q0=makeQuery(id+"F24.boolean.opBoolean","MERGE",FACE,{"derivedFrom":[makeQuery(id+"F16.opExtrude","SWEPT_FACE",FACE,{"disambiguationData":[OSD([sQuery(id+"F15.wireOp",EDGE,"E54.rect.top")])]}),makeQuery(id+"F24.opExtrude","SWEPT_FACE",FACE,{"disambiguationData":[OSD([sQuery(id+"F23.wireOp",EDGE,"E67.bottom")])]})]});
            var sketch = newSketch(context, id + "F25", { "sketchPlane" : qUnion([Q0])});
            skCircle(sketch, "E69.0.MirrorC", {"center": v(25, 25) * mm, "radius": 6 * mm});
            skCircle(sketch, "E70", {"center": v(-25, 25) * mm, "radius": 6 * mm});
            skSolve(sketch);
        }
        {
            var Q0;
            Q0=makeQuery(id+"F25.imprint","IMPRINT",FACE,{"disambiguationData":[TD([[makeQuery(id+"F25.imprint","IMPRINT",EDGE,{"derivedFrom":sQuery(id+"F25.wireOp",EDGE,"E70")}),1.0]])]});
            var Q1;
            Q1=makeQuery(id+"F25.imprint","IMPRINT",FACE,{"disambiguationData":[TD([[makeQuery(id+"F25.imprint","IMPRINT",EDGE,{"derivedFrom":sQuery(id+"F25.wireOp",EDGE,"E69.0.MirrorC")}),-1.0]])]});
            var Q2;
            Q2=makeQuery(id+"F24.boolean.opBoolean","MERGE",FACE,{"derivedFrom":[makeQuery(id+"F16.opExtrude","SWEPT_FACE",FACE,{"disambiguationData":[OSD([sQuery(id+"F15.wireOp",EDGE,"E54.rect.bottom")])]}),makeQuery(id+"F24.opExtrude","SWEPT_FACE",FACE,{"disambiguationData":[OSD([sQuery(id+"F23.wireOp",EDGE,"E68.1.MirrorCS")])]})]});
            extrude(context, id + "F26", {"entities" : qUnion([Q0, Q1]), "operationType" : NewBodyOperationType.REMOVE, "endBound" : BoundingType.UP_TO_SURFACE, "oppositeDirection" : true, "endBoundEntityFace" : qUnion([Q2]), "depth" : 300 * mm});
        }
        {
            var Q0;
            Q0=makeQuery(id+"F5.opExtrude","CAP_FACE",FACE,{"disambiguationData":[OSD([sQuery(id+"F0.wireOp",EDGE,"E0.rect.bottom"),sQuery(id+"F0.wireOp",EDGE,"E0.rect.top"),sQuery(id+"F0.wireOp",EDGE,"E17"),sQuery(id+"F0.wireOp",EDGE,"E18")])],"isStart":false});
            var sketch = newSketch(context, id + "F27", { "sketchPlane" : qUnion([Q0])});
            skLineSegment(sketch, "E71", {"start": v(-130, 0) * mm, "end": v(-130, -105) * mm});
            skLineSegment(sketch, "E72.0.MirrorCS", {"start": v(129.98, 0) * mm, "end": v(130, -105) * mm});
            skLineSegment(sketch, "E73", {"start": v(-130, -105) * mm, "end": v(130, -105) * mm});
            skLineSegment(sketch, "E74", {"start": v(-130, -462) * mm, "end": v(130.08, -462) * mm});
            skLineSegment(sketch, "E75", {"start": v(-130, 0) * mm, "end": v(129.98, 0) * mm, "construction": true});
            skLineSegment(sketch, "E76.0.MirrorCS", {"start": v(129.98, 0) * mm, "end": v(130, 105) * mm});
            skLineSegment(sketch, "E76.1.MirrorCS", {"start": v(-130, 0) * mm, "end": v(-130, 105) * mm});
            skLineSegment(sketch, "E76.2.MirrorCS", {"start": v(-130, 105) * mm, "end": v(130, 105) * mm});
            skLineSegment(sketch, "E76.3.MirrorCS", {"start": v(-130, 462) * mm, "end": v(130.08, 462) * mm});
            skLineSegment(sketch, "E77", {"start": v(-570, -554.94) * mm, "end": v(-570, 462) * mm});
            skLineSegment(sketch, "E78", {"start": v(570, -560.15) * mm, "end": v(570, 461.9) * mm});
            skLineSegment(sketch, "E79", {"start": v(-130, -462) * mm, "end": v(-570, -462) * mm});
            skLineSegment(sketch, "E80", {"start": v(130.08, -462) * mm, "end": v(570, -461.9) * mm});
            skLineSegment(sketch, "E81", {"start": v(-130, 462) * mm, "end": v(-570, 462) * mm});
            skLineSegment(sketch, "E82", {"start": v(130.08, 462) * mm, "end": v(570, 461.9) * mm});
            skLineSegment(sketch, "E83", {"start": v(0, 105) * mm, "end": v(0, 462) * mm});
            skLineSegment(sketch, "E84", {"start": v(0, -105) * mm, "end": v(0, -462) * mm});
            skLineSegment(sketch, "E85", {"start": v(130, -105) * mm, "end": v(130, 105) * mm});
            skSolve(sketch);
        }
        {
            var Q0;
            {var subQ3=makeQuery(id+"F5.opExtrude","CAP_EDGE",EDGE,{"disambiguationData":[OSD([sQuery(id+"F0.wireOp",EDGE,"E17")])],"isStart":false});Q0=makeQuery(id+"F27.imprint","IMPRINT",FACE,{"disambiguationData":[TD([[makeQuery(id+"F27.imprint","IMPRINT",EDGE,{"derivedFrom":subQ3}),-1.0]])]});}
            var Q1;
            {var subQ9=sQuery(id+"F27.wireOp",EDGE,"E79");Q1=makeQuery(id+"F27.imprint","IMPRINT",FACE,{"disambiguationData":[TD([[makeQuery(id+"F27.imprint","IMPRINT",EDGE,{"derivedFrom":subQ9}),-1.0]])]});}
            extrude(context, id + "F28", {"entities" : qUnion([Q0, Q1]), "depth" : 10 * mm});
        }
        {
            var Q0;
            {var subQ3=makeQuery(id+"F5.opExtrude","CAP_EDGE",EDGE,{"disambiguationData":[OSD([sQuery(id+"F0.wireOp",EDGE,"E18")])],"isStart":false});Q0=makeQuery(id+"F27.imprint","IMPRINT",FACE,{"disambiguationData":[TD([[makeQuery(id+"F27.imprint","IMPRINT",EDGE,{"derivedFrom":subQ3}),-1.0]])]});}
            var Q1;
            {var subQ13=sQuery(id+"F27.wireOp",EDGE,"E80");Q1=makeQuery(id+"F27.imprint","IMPRINT",FACE,{"disambiguationData":[TD([[makeQuery(id+"F27.imprint","IMPRINT",EDGE,{"derivedFrom":subQ13}),1.0]])]});}
            extrude(context, id + "F29", {"entities" : qUnion([Q0, Q1]), "depth" : 10 * mm});
        }
    });
